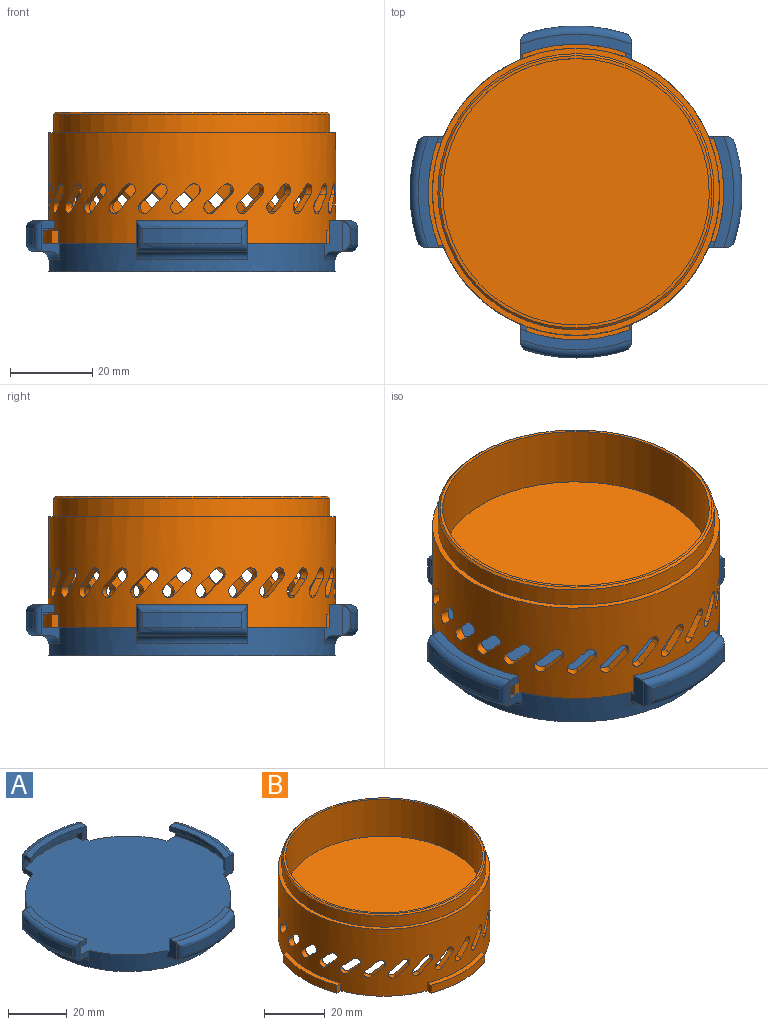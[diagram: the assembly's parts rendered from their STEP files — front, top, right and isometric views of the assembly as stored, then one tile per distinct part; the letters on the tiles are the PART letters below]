
ASSEMBLY  parts=2 mates=1
PART A: 62 faces, bbox 87.7x87.7x12.5 mm
  f0: cylinder r=35mm len=70mm, axis (0,0,-1), area 1095.9mm2, adj f1,f3,f7,f8,f19,f21,f22,f33
  f1: plane 77.24x77.24mm, normal (0,0,1), area 4232.4mm2, adj f0,f7,f8,f10,f11,f12,f21,f22
  f2: cylinder r=33.75mm len=67.5mm, axis (0,0,-1), area 954.3mm2, adj f4,f5
  f3: plane 70x70mm, normal (0,0,-1), area 163.2mm2, adj f0,f5
  f4: plane 67.5x67.5mm, normal (0,0,-1), area 3578.5mm2, adj f2
  f5: cone r=34.25mm half-angle=45deg, axis (0,0,-1), area 151.1mm2, adj f2,f3
  f6: cylinder r=40.5mm len=24.2mm, axis (0,0,1), area 86mm2, adj f15,f16,f17,f18
  f7: plane 9.51x4.46mm, normal (0,-1,0), area 18.4mm2, adj f0,f1,f9,f10,f12,f13,f14,f15
  f8: plane 9.51x4.46mm, normal (0,1,0), area 28mm2, adj f0,f1,f9,f12,f13,f15,f16,f18
  f9: plane 27x4.05mm, normal (0,0,-1), area 41.4mm2, adj f7,f8,f15,f19
  f10: cylinder r=38.62mm len=25.5mm, axis (0,0,-1), area 91mm2, adj f1,f7,f11,f14
  f11: plane 3.5x2.71mm, normal (0,-1,0), area 9.5mm2, adj f1,f10,f12,f14
  f12: cylinder r=36.06mm len=27mm, axis (0,0,-1), area 61mm2, adj f1,f7,f8,f11,f13,f14
  f13: plane 27x5.07mm, normal (0,0,1), area 67.5mm2, adj f7,f8,f12,f18
  f14: plane 25.5x5.19mm, normal (0,0,-1), area 66.7mm2, adj f7,f10,f11,f12
  f15: torus R=38.5mm, axis (0,0,1), area 84mm2, adj f6,f7,f8,f9,f16,f17
  f16: cylinder r=2mm len=7.29mm, axis (0,0,1), area 14.4mm2, adj f6,f8,f15,f18
  f17: cylinder r=2mm len=7.29mm, axis (0,0,1), area 14.4mm2, adj f6,f7,f15,f18
  f18: torus R=38.5mm, axis (0,0,1), area 84mm2, adj f6,f7,f8,f13,f16,f17
  f19: torus R=37mm, axis (0,0,1), area 87mm2, adj f0,f7,f8,f9
  f20: cylinder r=40.5mm len=24.2mm, axis (0,0,1), area 86mm2, adj f29,f30,f31,f32
  f21: plane 9.51x4.46mm, normal (-1,0,0), area 18.4mm2, adj f0,f1,f23,f24,f26,f27,f28,f29
  f22: plane 9.51x4.46mm, normal (1,0,0), area 28mm2, adj f0,f1,f23,f26,f27,f29,f30,f32
  f23: plane 27x4.05mm, normal (0,0,-1), area 41.4mm2, adj f21,f22,f29,f33
  f24: cylinder r=38.62mm len=25.5mm, axis (0,0,-1), area 91mm2, adj f1,f21,f25,f28
  f25: plane 3.5x2.71mm, normal (-1,0,0), area 9.5mm2, adj f1,f24,f26,f28
  f26: cylinder r=36.06mm len=27mm, axis (0,0,-1), area 61mm2, adj f1,f21,f22,f25,f27,f28
  f27: plane 27x5.07mm, normal (0,0,1), area 67.5mm2, adj f21,f22,f26,f32
  f28: plane 25.5x5.19mm, normal (0,0,-1), area 66.7mm2, adj f21,f24,f25,f26
  f29: torus R=38.5mm, axis (0,0,1), area 84mm2, adj f20,f21,f22,f23,f30,f31
  f30: cylinder r=2mm len=7.29mm, axis (0,0,1), area 14.4mm2, adj f20,f22,f29,f32
  f31: cylinder r=2mm len=7.29mm, axis (0,0,1), area 14.4mm2, adj f20,f21,f29,f32
  f32: torus R=38.5mm, axis (0,0,1), area 84mm2, adj f20,f21,f22,f27,f30,f31
  f33: torus R=37mm, axis (0,0,1), area 87mm2, adj f0,f21,f22,f23
  f34: cylinder r=40.5mm len=24.2mm, axis (0,0,1), area 86mm2, adj f43,f44,f45,f46
  f35: plane 9.51x4.46mm, normal (0,1,0), area 18.4mm2, adj f0,f1,f37,f38,f40,f41,f42,f43
  f36: plane 9.51x4.46mm, normal (0,-1,0), area 28mm2, adj f0,f1,f37,f40,f41,f43,f44,f46
  f37: plane 27x4.05mm, normal (0,0,-1), area 41.4mm2, adj f35,f36,f43,f47
  f38: cylinder r=38.62mm len=25.5mm, axis (0,0,-1), area 91mm2, adj f1,f35,f39,f42
  f39: plane 3.5x2.71mm, normal (0,1,0), area 9.5mm2, adj f1,f38,f40,f42
  f40: cylinder r=36.06mm len=27mm, axis (0,0,-1), area 61mm2, adj f1,f35,f36,f39,f41,f42
  f41: plane 27x5.07mm, normal (0,0,1), area 67.5mm2, adj f35,f36,f40,f46
  f42: plane 25.5x5.19mm, normal (0,0,-1), area 66.7mm2, adj f35,f38,f39,f40
  f43: torus R=38.5mm, axis (0,0,1), area 84mm2, adj f34,f35,f36,f37,f44,f45
  f44: cylinder r=2mm len=7.29mm, axis (0,0,1), area 14.4mm2, adj f34,f36,f43,f46
  f45: cylinder r=2mm len=7.29mm, axis (0,0,1), area 14.4mm2, adj f34,f35,f43,f46
  f46: torus R=38.5mm, axis (0,0,1), area 84mm2, adj f34,f35,f36,f41,f44,f45
  f47: torus R=37mm, axis (0,0,1), area 87mm2, adj f0,f35,f36,f37
  f48: cylinder r=40.5mm len=24.2mm, axis (0,0,1), area 86mm2, adj f57,f58,f59,f60
  f49: plane 9.51x4.46mm, normal (1,0,0), area 18.4mm2, adj f0,f1,f51,f52,f54,f55,f56,f57
  f50: plane 9.51x4.46mm, normal (-1,0,0), area 28mm2, adj f0,f1,f51,f54,f55,f57,f58,f60
  f51: plane 27x4.05mm, normal (0,0,-1), area 41.4mm2, adj f49,f50,f57,f61
  f52: cylinder r=38.62mm len=25.5mm, axis (0,0,-1), area 91mm2, adj f1,f49,f53,f56
  f53: plane 3.5x2.71mm, normal (1,0,0), area 9.5mm2, adj f1,f52,f54,f56
  f54: cylinder r=36.06mm len=27mm, axis (0,0,-1), area 61mm2, adj f1,f49,f50,f53,f55,f56
  f55: plane 27x5.07mm, normal (0,0,1), area 67.5mm2, adj f49,f50,f54,f60
  f56: plane 25.5x5.19mm, normal (0,0,-1), area 66.7mm2, adj f49,f52,f53,f54
  f57: torus R=38.5mm, axis (0,0,1), area 84mm2, adj f48,f49,f50,f51,f58,f59
  f58: cylinder r=2mm len=7.29mm, axis (0,0,1), area 14.4mm2, adj f48,f50,f57,f60
  f59: cylinder r=2mm len=7.29mm, axis (0,0,1), area 14.4mm2, adj f48,f49,f57,f60
  f60: torus R=38.5mm, axis (0,0,1), area 84mm2, adj f48,f49,f50,f55,f58,f59
  f61: torus R=37mm, axis (0,0,1), area 87mm2, adj f0,f49,f50,f51
PART B: 134 faces, bbox 73.5x73.5x32 mm
  f0: cylinder r=35mm len=70mm, axis (0,0,-1), area 4929.7mm2, adj f5,f8,f11,f12,f13,f14,f16,f17
  f1: plane 66.38x66.38mm, normal (0,0,1), area 142.4mm2, adj f2,f6
  f2: cylinder r=32.5mm len=65mm, axis (0,0,-1), area 3063.1mm2, adj f1,f3
  f3: plane 65x65mm, normal (0,0,1), area 3318.3mm2, adj f2
  f4: cylinder r=33.69mm len=67.38mm, axis (0,0,1), area 952.6mm2, adj f5,f6
  f5: plane 70x70mm, normal (0,0,1), area 282.7mm2, adj f0,f4
  f6: cone r=33.19mm half-angle=45deg, axis (0,0,-1), area 148.6mm2, adj f1,f4
  f7: cylinder r=33mm len=66mm, axis (0,0,1), area 2432.3mm2, adj f8,f9,f26,f27,f28,f29,f30,f31
  f8: plane 73.5x73.5mm, normal (0,0,-1), area 606mm2, adj f0,f7,f10,f11,f12,f14,f15,f16
  f9: plane 66x66mm, normal (0,0,-1), area 3421.2mm2, adj f7
  f10: cylinder r=36.75mm len=25mm, axis (0,0,-1), area 81.6mm2, adj f8,f11,f12,f13
  f11: plane 3.2x1.87mm, normal (-1,0,0), area 6mm2, adj f0,f8,f10,f13
  f12: plane 3.2x1.87mm, normal (1,0,0), area 6mm2, adj f0,f8,f10,f13
  f13: plane 25x4.06mm, normal (0,0,1), area 44.7mm2, adj f0,f10,f11,f12
  f14: plane 3.2x1.87mm, normal (0,-1,0), area 6mm2, adj f0,f8,f15,f17
  f15: cylinder r=36.75mm len=25mm, axis (0,0,-1), area 81.6mm2, adj f8,f14,f16,f17
  f16: plane 3.2x1.87mm, normal (0,1,0), area 6mm2, adj f0,f8,f15,f17
  f17: plane 25x4.06mm, normal (0,0,1), area 44.7mm2, adj f0,f14,f15,f16
  f18: plane 3.2x1.87mm, normal (-1,0,0), area 6mm2, adj f0,f8,f19,f21
  f19: cylinder r=36.75mm len=25mm, axis (0,0,-1), area 81.6mm2, adj f8,f18,f20,f21
  f20: plane 3.2x1.87mm, normal (1,0,0), area 6mm2, adj f0,f8,f19,f21
  f21: plane 25x4.06mm, normal (0,0,1), area 44.7mm2, adj f0,f18,f19,f20
  f22: plane 3.2x1.87mm, normal (0,1,0), area 6mm2, adj f0,f8,f23,f25
  f23: cylinder r=36.75mm len=25mm, axis (0,0,-1), area 81.6mm2, adj f8,f22,f24,f25
  f24: plane 3.2x1.87mm, normal (0,-1,0), area 6mm2, adj f0,f8,f23,f25
  f25: plane 25x4.06mm, normal (0,0,1), area 44.7mm2, adj f0,f22,f23,f24
  f26: cylinder r=1.5mm len=2.56mm, axis (0,-1,0), area 9.4mm2, adj f0,f7,f27,f29
  f27: plane 4.18x4.18mm, normal (0.71,0,0.71), area 11.8mm2, adj f0,f7,f26,f28
  f28: cylinder r=1.5mm len=2.62mm, axis (0,-1,0), area 9.7mm2, adj f0,f7,f27,f29
  f29: plane 4.26x4.26mm, normal (-0.71,0,-0.71), area 12.1mm2, adj f0,f7,f26,f28
  f30: cylinder r=1.5mm len=2.95mm, axis (-0.23,-0.97,0), area 9.4mm2, adj f0,f7,f31,f33
  f31: plane 4.5x4.18mm, normal (0.69,-0.16,0.71), area 11.8mm2, adj f0,f7,f30,f32
  f32: cylinder r=1.5mm len=3.1mm, axis (-0.23,-0.97,0), area 9.7mm2, adj f0,f7,f31,f33
  f33: plane 4.51x4.26mm, normal (-0.69,0.16,-0.71), area 12.1mm2, adj f0,f7,f30,f32
  f34: cylinder r=1.5mm len=3.19mm, axis (-0.45,-0.89,0), area 9.4mm2, adj f0,f7,f35,f37
  f35: plane 4.58x4.18mm, normal (0.63,-0.32,0.71), area 11.8mm2, adj f0,f7,f34,f36
  f36: cylinder r=1.5mm len=3.41mm, axis (-0.45,-0.89,0), area 9.7mm2, adj f0,f7,f35,f37
  f37: plane 4.53x4.26mm, normal (-0.63,0.32,-0.71), area 12.1mm2, adj f0,f7,f34,f36
  f38: cylinder r=1.5mm len=3.25mm, axis (-0.64,-0.77,0), area 9.4mm2, adj f0,f7,f39,f41
  f39: plane 4.41x4.32mm, normal (0.54,-0.45,0.71), area 11.8mm2, adj f0,f7,f38,f40
  f40: cylinder r=1.5mm len=3.53mm, axis (-0.64,-0.77,0), area 9.7mm2, adj f0,f7,f39,f41
  f41: plane 4.59x4.3mm, normal (-0.54,0.45,-0.71), area 12.1mm2, adj f0,f7,f38,f40
  f42: cylinder r=1.5mm len=3.25mm, axis (-0.8,-0.6,0), area 9.4mm2, adj f0,f7,f43,f45
  f43: plane 4.63x4.18mm, normal (0.42,-0.57,0.71), area 11.8mm2, adj f0,f7,f42,f44
  f44: cylinder r=1.5mm len=3.52mm, axis (-0.8,-0.6,0), area 9.7mm2, adj f0,f7,f43,f45
  f45: plane 4.86x4.26mm, normal (-0.42,0.57,-0.71), area 12.1mm2, adj f0,f7,f42,f44
  f46: cylinder r=1.5mm len=3.14mm, axis (-0.92,-0.4,0), area 9.4mm2, adj f0,f7,f47,f49
  f47: plane 4.69x4.18mm, normal (0.28,-0.65,0.71), area 11.8mm2, adj f0,f7,f46,f48
  f48: cylinder r=1.5mm len=3.35mm, axis (-0.92,-0.4,0), area 9.7mm2, adj f0,f7,f47,f49
  f49: plane 4.86x4.26mm, normal (-0.28,0.65,-0.71), area 12.1mm2, adj f0,f7,f46,f48
  f50: cylinder r=1.5mm len=2.87mm, axis (-0.98,-0.17,0), area 9.4mm2, adj f0,f7,f51,f53
  f51: plane 4.49x4.18mm, normal (0.12,-0.7,0.71), area 11.8mm2, adj f0,f7,f50,f52
  f52: cylinder r=1.5mm len=2.99mm, axis (-0.98,-0.17,0), area 9.7mm2, adj f0,f7,f51,f53
  f53: plane 4.61x4.26mm, normal (-0.12,0.7,-0.71), area 12.1mm2, adj f0,f7,f50,f52
  f54: cylinder r=1.5mm len=2.67mm, axis (-1,0.06,0), area 9.4mm2, adj f0,f7,f55,f57
  f55: plane 4.29x4.18mm, normal (-0.04,-0.71,0.71), area 11.8mm2, adj f0,f7,f54,f56
  f56: cylinder r=1.5mm len=2.76mm, axis (-1,0.06,0), area 9.7mm2, adj f0,f7,f55,f57
  f57: plane 4.34x4.26mm, normal (0.04,0.71,-0.71), area 12.1mm2, adj f0,f7,f54,f56
  f58: cylinder r=1.5mm len=3.03mm, axis (-0.96,0.29,0), area 9.4mm2, adj f0,f7,f59,f61
  f59: plane 4.55x4.18mm, normal (-0.2,-0.68,0.71), area 11.8mm2, adj f0,f7,f58,f60
  f60: cylinder r=1.5mm len=3.19mm, axis (-0.96,0.29,0), area 9.7mm2, adj f0,f7,f59,f61
  f61: plane 4.54x4.26mm, normal (0.2,0.68,-0.71), area 12.1mm2, adj f0,f7,f58,f60
  f62: cylinder r=1.5mm len=3.22mm, axis (-0.87,0.5,0), area 9.4mm2, adj f0,f7,f63,f65
  f63: plane 4.56x4.18mm, normal (-0.35,-0.61,0.71), area 11.8mm2, adj f0,f7,f62,f64
  f64: cylinder r=1.5mm len=3.45mm, axis (-0.87,0.5,0), area 9.7mm2, adj f0,f7,f63,f65
  f65: plane 4.49x4.26mm, normal (0.35,0.61,-0.71), area 12.1mm2, adj f0,f7,f62,f64
  f66: cylinder r=1.5mm len=3.24mm, axis (-0.73,0.69,0), area 9.4mm2, adj f0,f7,f67,f69
  f67: plane 4.42x4.33mm, normal (-0.49,-0.51,0.71), area 11.8mm2, adj f0,f7,f66,f68
  f68: cylinder r=1.5mm len=3.53mm, axis (-0.73,0.69,0), area 9.7mm2, adj f0,f7,f67,f69
  f69: plane 4.68x4.26mm, normal (0.49,0.51,-0.71), area 12.1mm2, adj f0,f7,f66,f68
  f70: cylinder r=1.5mm len=3.24mm, axis (-0.55,0.84,0), area 9.4mm2, adj f0,f7,f71,f73
  f71: plane 4.67x4.18mm, normal (-0.59,-0.39,0.71), area 11.8mm2, adj f0,f7,f70,f72
  f72: cylinder r=1.5mm len=3.49mm, axis (-0.55,0.84,0), area 9.7mm2, adj f0,f7,f71,f73
  f73: plane 4.88x4.26mm, normal (0.59,0.39,-0.71), area 12.1mm2, adj f0,f7,f70,f72
  f74: cylinder r=1.5mm len=3.09mm, axis (-0.34,0.94,0), area 9.4mm2, adj f0,f7,f75,f77
  f75: plane 4.66x4.18mm, normal (-0.66,-0.24,0.71), area 11.8mm2, adj f0,f7,f74,f76
  f76: cylinder r=1.5mm len=3.27mm, axis (-0.34,0.94,0), area 9.7mm2, adj f0,f7,f75,f77
  f77: plane 4.83x4.26mm, normal (0.66,0.24,-0.71), area 12.1mm2, adj f0,f7,f74,f76
  f78: cylinder r=1.5mm len=2.78mm, axis (-0.12,0.99,0), area 9.4mm2, adj f0,f7,f79,f81
  f79: plane 4.4x4.18mm, normal (-0.7,-0.08,0.71), area 11.8mm2, adj f0,f7,f78,f80
  f80: cylinder r=1.5mm len=2.88mm, axis (-0.12,0.99,0), area 9.7mm2, adj f0,f7,f79,f81
  f81: plane 4.51x4.26mm, normal (0.7,0.08,-0.71), area 12.1mm2, adj f0,f7,f78,f80
  f82: cylinder r=1.5mm len=2.78mm, axis (0.12,0.99,0), area 9.4mm2, adj f0,f7,f83,f85
  f83: plane 4.37x4.18mm, normal (-0.7,0.08,0.71), area 11.8mm2, adj f0,f7,f82,f84
  f84: cylinder r=1.5mm len=2.88mm, axis (0.12,0.99,0), area 9.7mm2, adj f0,f7,f83,f85
  f85: plane 4.41x4.26mm, normal (0.7,-0.08,-0.71), area 12.1mm2, adj f0,f7,f82,f84
  f86: cylinder r=1.5mm len=3.09mm, axis (0.34,0.94,0), area 9.4mm2, adj f0,f7,f87,f89
  f87: plane 4.57x4.18mm, normal (-0.66,0.24,0.71), area 11.8mm2, adj f0,f7,f86,f88
  f88: cylinder r=1.5mm len=3.27mm, axis (0.34,0.94,0), area 9.7mm2, adj f0,f7,f87,f89
  f89: plane 4.55x4.26mm, normal (0.66,-0.24,-0.71), area 12.1mm2, adj f0,f7,f86,f88
  f90: cylinder r=1.5mm len=3.24mm, axis (0.55,0.84,0), area 9.4mm2, adj f0,f7,f91,f93
  f91: plane 4.53x4.18mm, normal (-0.59,0.39,0.71), area 11.8mm2, adj f0,f7,f90,f92
  f92: cylinder r=1.5mm len=3.49mm, axis (0.55,0.84,0), area 9.7mm2, adj f0,f7,f91,f93
  f93: plane 4.44x4.36mm, normal (0.59,-0.39,-0.71), area 12.1mm2, adj f0,f7,f90,f92
  f94: cylinder r=1.5mm len=3.24mm, axis (0.73,0.69,0), area 9.4mm2, adj f0,f7,f95,f97
  f95: plane 4.51x4.24mm, normal (-0.49,0.51,0.71), area 11.8mm2, adj f0,f7,f94,f96
  f96: cylinder r=1.5mm len=3.53mm, axis (0.73,0.69,0), area 9.7mm2, adj f0,f7,f95,f97
  f97: plane 4.76x4.26mm, normal (0.49,-0.51,-0.71), area 12.1mm2, adj f0,f7,f94,f96
  f98: cylinder r=1.5mm len=3.22mm, axis (0.87,0.5,0), area 9.4mm2, adj f0,f7,f99,f101
  f99: plane 4.69x4.18mm, normal (-0.35,0.61,0.71), area 11.8mm2, adj f0,f7,f98,f100
  f100: cylinder r=1.5mm len=3.45mm, axis (0.87,0.5,0), area 9.7mm2, adj f0,f7,f99,f101
  f101: plane 4.89x4.26mm, normal (0.35,-0.61,-0.71), area 12.1mm2, adj f0,f7,f98,f100
  f102: cylinder r=1.5mm len=3.03mm, axis (0.96,0.29,0), area 9.4mm2, adj f0,f7,f103,f105
  f103: plane 4.62x4.18mm, normal (-0.2,0.68,0.71), area 11.8mm2, adj f0,f7,f102,f104
  f104: cylinder r=1.5mm len=3.19mm, axis (0.96,0.29,0), area 9.7mm2, adj f0,f7,f103,f105
  f105: plane 4.77x4.26mm, normal (0.2,-0.68,-0.71), area 12.1mm2, adj f0,f7,f102,f104
  f106: cylinder r=1.5mm len=2.67mm, axis (1,0.06,0), area 9.4mm2, adj f0,f7,f107,f109
  f107: plane 4.3x4.18mm, normal (-0.04,0.71,0.71), area 11.8mm2, adj f0,f7,f106,f108
  f108: cylinder r=1.5mm len=2.76mm, axis (1,0.06,0), area 9.7mm2, adj f0,f7,f107,f109
  f109: plane 4.39x4.26mm, normal (0.04,-0.71,-0.71), area 12.1mm2, adj f0,f7,f106,f108
  f110: cylinder r=1.5mm len=2.87mm, axis (0.98,-0.17,0), area 9.4mm2, adj f0,f7,f111,f113
  f111: plane 4.45x4.18mm, normal (0.12,0.7,0.71), area 11.8mm2, adj f0,f7,f110,f112
  f112: cylinder r=1.5mm len=2.99mm, axis (0.98,-0.17,0), area 9.7mm2, adj f0,f7,f111,f113
  f113: plane 4.47x4.26mm, normal (-0.12,-0.7,-0.71), area 12.1mm2, adj f0,f7,f110,f112
  f114: cylinder r=1.5mm len=3.14mm, axis (0.92,-0.4,0), area 9.4mm2, adj f0,f7,f115,f117
  f115: plane 4.59x4.18mm, normal (0.28,0.65,0.71), area 11.8mm2, adj f0,f7,f114,f116
  f116: cylinder r=1.5mm len=3.35mm, axis (0.92,-0.4,0), area 9.7mm2, adj f0,f7,f115,f117
  f117: plane 4.55x4.26mm, normal (-0.28,-0.65,-0.71), area 12.1mm2, adj f0,f7,f114,f116
  f118: cylinder r=1.5mm len=3.25mm, axis (0.8,-0.6,0), area 9.4mm2, adj f0,f7,f119,f121
  f119: plane 4.48x4.21mm, normal (0.42,0.57,0.71), area 11.8mm2, adj f0,f7,f118,f120
  f120: cylinder r=1.5mm len=3.52mm, axis (0.8,-0.6,0), area 9.7mm2, adj f0,f7,f119,f121
  f121: plane 4.48x4.38mm, normal (-0.42,-0.57,-0.71), area 12.1mm2, adj f0,f7,f118,f120
  f122: cylinder r=1.5mm len=3.25mm, axis (0.64,-0.77,0), area 9.4mm2, adj f0,f7,f123,f125
  f123: plane 4.58x4.18mm, normal (0.54,0.45,0.71), area 11.8mm2, adj f0,f7,f122,f124
  f124: cylinder r=1.5mm len=3.53mm, axis (0.64,-0.77,0), area 9.7mm2, adj f0,f7,f123,f125
  f125: plane 4.81x4.26mm, normal (-0.54,-0.45,-0.71), area 12.1mm2, adj f0,f7,f122,f124
  f126: cylinder r=1.5mm len=3.19mm, axis (0.45,-0.89,0), area 9.4mm2, adj f0,f7,f127,f129
  f127: plane 4.7x4.18mm, normal (0.63,0.32,0.71), area 11.8mm2, adj f0,f7,f126,f128
  f128: cylinder r=1.5mm len=3.41mm, axis (0.45,-0.89,0), area 9.7mm2, adj f0,f7,f127,f129
  f129: plane 4.89x4.26mm, normal (-0.63,-0.32,-0.71), area 12.1mm2, adj f0,f7,f126,f128
  f130: cylinder r=1.5mm len=2.95mm, axis (0.23,-0.97,0), area 9.4mm2, adj f0,f7,f131,f133
  f131: plane 4.56x4.18mm, normal (0.69,0.16,0.71), area 11.8mm2, adj f0,f7,f130,f132
  f132: cylinder r=1.5mm len=3.1mm, axis (0.23,-0.97,0), area 9.7mm2, adj f0,f7,f131,f133
  f133: plane 4.7x4.26mm, normal (-0.69,-0.16,-0.71), area 12.1mm2, adj f0,f7,f130,f132
PLACE A t=(0,0,-17)mm
PLACE B rot(axis=(0,0,-1),179.1deg) t=(0,0,17)mm
MATE revolute B.f0 <-> A.f0  axis (0,0,-1) through (0,0,0)mm
